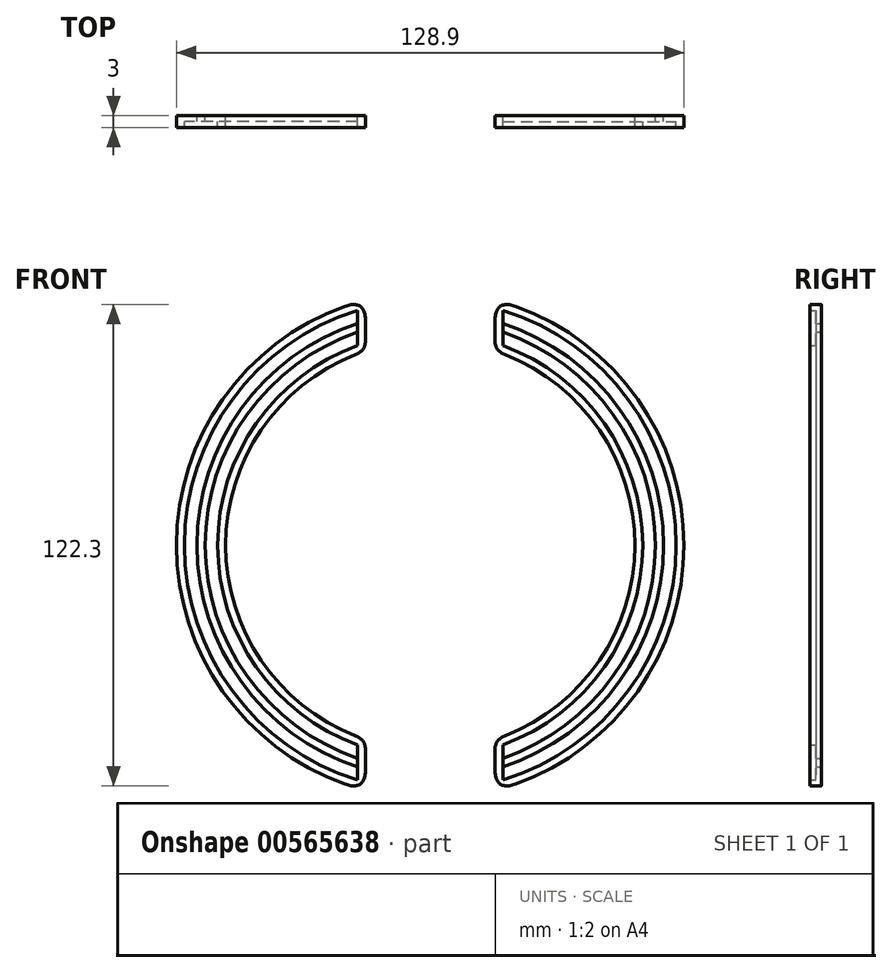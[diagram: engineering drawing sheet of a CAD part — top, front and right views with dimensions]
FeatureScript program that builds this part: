
annotation { "Feature Type Name" : "Feature", "Feature Type Description" : "" }
export const myFeature = defineFeature(function(context is Context, id is Id, definition is map)
    precondition{}
    {
        {
            var Q0;
            Q0=qCreatedBy(makeId("Front.planeOp"),FACE);
            var sketch = newSketch(context, id + "F0", { "sketchPlane" : qUnion([Q0])});
            skArc(sketch, "E0", {"start": v(-16.43, 51.43) * mm, "mid": v(-53.99, 0) * mm, "end": v(-16.43, -51.43) * mm, "construction": true});
            skLineSegment(sketch, "E1", {"start": v(53.99, 0) * mm, "end": v(-53.99, 0) * mm, "construction": true});
            skArc(sketch, "E2", {"start": v(-16.43, 51.43) * mm, "mid": v(-53.99, 0) * mm, "end": v(-16.43, -51.43) * mm});
            skArc(sketch, "E3.0", {"start": v(-16.43, 54.75) * mm, "mid": v(-57.16, 0) * mm, "end": v(-16.43, -54.75) * mm});
            skArc(sketch, "E4", {"start": v(16.43, -51.43) * mm, "mid": v(53.99, 0) * mm, "end": v(16.43, 51.43) * mm});
            skArc(sketch, "E5.0", {"start": v(16.43, -54.75) * mm, "mid": v(57.16, 0) * mm, "end": v(16.43, 54.75) * mm});
            skArc(sketch, "E6.0", {"start": v(-16.43, 56.96) * mm, "mid": v(-59.28, 0) * mm, "end": v(-16.43, -56.96) * mm});
            skArc(sketch, "E7.0", {"start": v(16.43, -56.96) * mm, "mid": v(59.28, 0) * mm, "end": v(16.43, 56.96) * mm});
            skArc(sketch, "E8.0", {"start": v(-16.43, 60.25) * mm, "mid": v(-62.45, 0) * mm, "end": v(-16.43, -60.25) * mm});
            skArc(sketch, "E8.1", {"start": v(16.43, -60.25) * mm, "mid": v(62.45, 0) * mm, "end": v(16.43, 60.25) * mm});
            skArc(sketch, "E9.0", {"start": v(-16.43, 49.32) * mm, "mid": v(-51.99, 0) * mm, "end": v(-16.43, -49.32) * mm});
            skArc(sketch, "E10.0", {"start": v(-16.43, 62.33) * mm, "mid": v(-64.45, 0) * mm, "end": v(-16.43, -62.33) * mm});
            skArc(sketch, "E11.MirrorCS", {"start": v(16.43, 51.43) * mm, "mid": v(53.99, 0) * mm, "end": v(16.43, -51.43) * mm});
            skArc(sketch, "E12.MirrorCS", {"start": v(16.43, 56.96) * mm, "mid": v(59.28, 0) * mm, "end": v(16.43, -56.96) * mm});
            skArc(sketch, "E13.MirrorCS", {"start": v(16.43, 62.33) * mm, "mid": v(64.45, 0) * mm, "end": v(16.43, -62.33) * mm});
            skArc(sketch, "E14.MirrorCS", {"start": v(16.43, 49.32) * mm, "mid": v(51.99, 0) * mm, "end": v(16.43, -49.32) * mm});
            skArc(sketch, "E15.MirrorCS", {"start": v(16.43, 60.25) * mm, "mid": v(62.45, 0) * mm, "end": v(16.43, -60.25) * mm});
            skArc(sketch, "E16.MirrorCS", {"start": v(16.43, 54.75) * mm, "mid": v(57.16, 0) * mm, "end": v(16.43, -54.75) * mm});
            skLineSegment(sketch, "E17.left", {"start": v(-16.43, 62.33) * mm, "end": v(-16.43, 49.32) * mm});
            skLineSegment(sketch, "E17.right", {"start": v(16.43, 62.33) * mm, "end": v(16.43, 49.32) * mm});
            skPoint(sketch, "E18.orphan", {"position": v(-16.43, 64.45) * mm});
            skLineSegment(sketch, "E19.trimOffspring", {"start": v(0, 0) * mm, "end": v(0, -53.99) * mm, "construction": true});
            skArc(sketch, "E20.trimOffspring", {"start": v(16.43, -51.43) * mm, "mid": v(53.99, 0) * mm, "end": v(16.43, 51.43) * mm, "construction": true});
            skLineSegment(sketch, "E21.trimOffspring", {"start": v(-16.43, -49.32) * mm, "end": v(-16.43, -62.33) * mm});
            skLineSegment(sketch, "E22.trimOffspring", {"start": v(16.43, -49.32) * mm, "end": v(16.43, -60.25) * mm});
            skLineSegment(sketch, "E23", {"start": v(16.43, -60.25) * mm, "end": v(16.43, -62.33) * mm});
            skLineSegment(sketch, "E24.right", {"start": v(-18.43, 61.76) * mm, "end": v(-18.43, 48.61) * mm});
            skLineSegment(sketch, "E25.MirrorCS", {"start": v(18.43, 61.76) * mm, "end": v(18.43, 48.61) * mm});
            skPoint(sketch, "E26.orphan", {"position": v(-18.43, -62.33) * mm});
            skPoint(sketch, "E27.orphan", {"position": v(18.43, -62.33) * mm});
            skPoint(sketch, "E28.orphan", {"position": v(-18.43, 62.33) * mm});
            skPoint(sketch, "E29.orphan", {"position": v(18.43, 62.33) * mm});
            skLineSegment(sketch, "E30.trimOffspring", {"start": v(-18.43, 0) * mm, "end": v(-18.43, -61.76) * mm});
            skLineSegment(sketch, "E31.trimOffspring", {"start": v(-16.43, 0) * mm, "end": v(-16.43, -62.33) * mm});
            skLineSegment(sketch, "E32.trimOffspring", {"start": v(16.43, 0) * mm, "end": v(16.43, -62.33) * mm});
            skLineSegment(sketch, "E33.trimOffspring", {"start": v(18.43, 0) * mm, "end": v(18.43, -61.76) * mm});
            skSolve(sketch);
        }
        {
            var Q0;
            {var subQ0=sQuery(id+"F0.wireOp",EDGE,"E6.0");Q0=makeQuery(id+"F0.imprint","IMPRINT",FACE,{"disambiguationData":[TD([[makeQuery(id+"F0.imprint","IMPRINT",EDGE,{"derivedFrom":subQ0}),-1.0]])]});}
            var Q1;
            {var subQ0=sQuery(id+"F0.wireOp",EDGE,"E2");Q1=makeQuery(id+"F0.imprint","IMPRINT",FACE,{"disambiguationData":[TD([[makeQuery(id+"F0.imprint","IMPRINT",EDGE,{"derivedFrom":subQ0}),-1.0]])]});}
            var Q2;
            {var subQ0=sQuery(id+"F0.wireOp",EDGE,"E7.0");Q2=makeQuery(id+"F0.imprint","IMPRINT",FACE,{"disambiguationData":[TD([[makeQuery(id+"F0.imprint","IMPRINT",EDGE,{"derivedFrom":subQ0}),-1.0]])]});}
            var Q3;
            {var subQ0=sQuery(id+"F0.wireOp",EDGE,"E4");Q3=makeQuery(id+"F0.imprint","IMPRINT",FACE,{"disambiguationData":[TD([[makeQuery(id+"F0.imprint","IMPRINT",EDGE,{"derivedFrom":subQ0}),-1.0]])]});}
            extrude(context, id + "F1", {"entities" : qUnion([Q0, Q1, Q2, Q3]), "depth" : 1.5 * mm, "offsetDistance" : 25 * mm});
        }
        {
            var Q0;
            {var subQ0=sQuery(id+"F0.wireOp",EDGE,"E8.0");Q0=makeQuery(id+"F0.imprint","IMPRINT",FACE,{"disambiguationData":[TD([[makeQuery(id+"F0.imprint","IMPRINT",EDGE,{"derivedFrom":subQ0}),-1.0]])]});}
            var Q1;
            {var subQ0=sQuery(id+"F0.wireOp",EDGE,"E2");Q1=makeQuery(id+"F0.imprint","IMPRINT",FACE,{"disambiguationData":[TD([[makeQuery(id+"F0.imprint","IMPRINT",EDGE,{"derivedFrom":subQ0}),1.0]])]});}
            var Q2;
            {var subQ0=sQuery(id+"F0.wireOp",EDGE,"E4");Q2=makeQuery(id+"F0.imprint","IMPRINT",FACE,{"disambiguationData":[TD([[makeQuery(id+"F0.imprint","IMPRINT",EDGE,{"derivedFrom":subQ0}),1.0]])]});}
            var Q3;
            {var subQ0=sQuery(id+"F0.wireOp",EDGE,"E8.1");Q3=makeQuery(id+"F0.imprint","IMPRINT",FACE,{"disambiguationData":[TD([[makeQuery(id+"F0.imprint","IMPRINT",EDGE,{"derivedFrom":subQ0}),-1.0]])]});}
            var Q4;
            {var subQ0=sQuery(id+"F0.wireOp",EDGE,"E17.left");var subQ1=sQuery(id+"F0.wireOp",EDGE,"E3.0");var subQ2=makeQuery(id+"F0.imprint","INTERSECT",VERTEX,{"derivedFrom":[subQ1,subQ0]});Q4=makeQuery(id+"F0.imprint","IMPRINT",FACE,{"disambiguationData":[TD([[makeQuery(id+"F0.imprint","IMPRINT",EDGE,{"disambiguationData":[TD([[subQ2,-1.0]])],"derivedFrom":subQ1}),-1.0]])]});}
            var Q5;
            {var subQ0=sQuery(id+"F0.wireOp",EDGE,"E17.right");var subQ1=sQuery(id+"F0.wireOp",EDGE,"E5.0");var subQ2=makeQuery(id+"F0.imprint","INTERSECT",VERTEX,{"derivedFrom":[subQ1,subQ0]});Q5=makeQuery(id+"F0.imprint","IMPRINT",FACE,{"disambiguationData":[TD([[makeQuery(id+"F0.imprint","IMPRINT",EDGE,{"disambiguationData":[TD([[subQ2,1.0]])],"derivedFrom":subQ1}),-1.0]])]});}
            var Q6;
            {var subQ0=sQuery(id+"F0.wireOp",EDGE,"E17.left");var subQ1=sQuery(id+"F0.wireOp",EDGE,"E2");var subQ2=makeQuery(id+"F0.imprint","INTERSECT",VERTEX,{"derivedFrom":[subQ1,subQ0]});Q6=makeQuery(id+"F0.imprint","IMPRINT",FACE,{"disambiguationData":[TD([[makeQuery(id+"F0.imprint","IMPRINT",EDGE,{"disambiguationData":[TD([[subQ2,-1.0]])],"derivedFrom":subQ1}),-1.0]])]});}
            var Q7;
            {var subQ0=sQuery(id+"F0.wireOp",EDGE,"E17.left");var subQ1=sQuery(id+"F0.wireOp",EDGE,"E6.0");var subQ2=makeQuery(id+"F0.imprint","INTERSECT",VERTEX,{"derivedFrom":[subQ1,subQ0]});Q7=makeQuery(id+"F0.imprint","IMPRINT",FACE,{"disambiguationData":[TD([[makeQuery(id+"F0.imprint","IMPRINT",EDGE,{"disambiguationData":[TD([[subQ2,-1.0]])],"derivedFrom":subQ1}),-1.0]])]});}
            var Q8;
            {var subQ0=sQuery(id+"F0.wireOp",EDGE,"E17.right");var subQ1=sQuery(id+"F0.wireOp",EDGE,"E7.0");var subQ2=makeQuery(id+"F0.imprint","INTERSECT",VERTEX,{"derivedFrom":[subQ1,subQ0]});Q8=makeQuery(id+"F0.imprint","IMPRINT",FACE,{"disambiguationData":[TD([[makeQuery(id+"F0.imprint","IMPRINT",EDGE,{"disambiguationData":[TD([[subQ2,1.0]])],"derivedFrom":subQ1}),-1.0]])]});}
            var Q9;
            {var subQ0=sQuery(id+"F0.wireOp",EDGE,"E17.right");var subQ1=sQuery(id+"F0.wireOp",EDGE,"E4");var subQ2=makeQuery(id+"F0.imprint","INTERSECT",VERTEX,{"derivedFrom":[subQ1,subQ0]});Q9=makeQuery(id+"F0.imprint","IMPRINT",FACE,{"disambiguationData":[TD([[makeQuery(id+"F0.imprint","IMPRINT",EDGE,{"disambiguationData":[TD([[subQ2,1.0]])],"derivedFrom":subQ1}),-1.0]])]});}
            var Q10;
            {var subQ0=sQuery(id+"F0.wireOp",EDGE,"E21.trimOffspring");var subQ1=sQuery(id+"F0.wireOp",EDGE,"E2");var subQ2=makeQuery(id+"F0.imprint","INTERSECT",VERTEX,{"derivedFrom":[subQ1,subQ0]});Q10=makeQuery(id+"F0.imprint","IMPRINT",FACE,{"disambiguationData":[TD([[makeQuery(id+"F0.imprint","IMPRINT",EDGE,{"disambiguationData":[TD([[subQ2,1.0]])],"derivedFrom":subQ1}),-1.0]])]});}
            var Q11;
            {var subQ0=sQuery(id+"F0.wireOp",EDGE,"E21.trimOffspring");var subQ1=sQuery(id+"F0.wireOp",EDGE,"E3.0");var subQ2=makeQuery(id+"F0.imprint","INTERSECT",VERTEX,{"derivedFrom":[subQ1,subQ0]});Q11=makeQuery(id+"F0.imprint","IMPRINT",FACE,{"disambiguationData":[TD([[makeQuery(id+"F0.imprint","IMPRINT",EDGE,{"disambiguationData":[TD([[subQ2,1.0]])],"derivedFrom":subQ1}),-1.0]])]});}
            var Q12;
            {var subQ0=sQuery(id+"F0.wireOp",EDGE,"E21.trimOffspring");var subQ1=sQuery(id+"F0.wireOp",EDGE,"E6.0");var subQ2=makeQuery(id+"F0.imprint","INTERSECT",VERTEX,{"derivedFrom":[subQ1,subQ0]});Q12=makeQuery(id+"F0.imprint","IMPRINT",FACE,{"disambiguationData":[TD([[makeQuery(id+"F0.imprint","IMPRINT",EDGE,{"disambiguationData":[TD([[subQ2,1.0]])],"derivedFrom":subQ1}),-1.0]])]});}
            var Q13;
            {var subQ0=sQuery(id+"F0.wireOp",EDGE,"E22.trimOffspring");var subQ1=sQuery(id+"F0.wireOp",EDGE,"E5.0");var subQ2=makeQuery(id+"F0.imprint","INTERSECT",VERTEX,{"derivedFrom":[subQ1,subQ0]});Q13=makeQuery(id+"F0.imprint","IMPRINT",FACE,{"disambiguationData":[TD([[makeQuery(id+"F0.imprint","IMPRINT",EDGE,{"disambiguationData":[TD([[subQ2,-1.0]])],"derivedFrom":subQ1}),-1.0]])]});}
            var Q14;
            {var subQ0=sQuery(id+"F0.wireOp",EDGE,"E22.trimOffspring");var subQ1=sQuery(id+"F0.wireOp",EDGE,"E4");var subQ2=makeQuery(id+"F0.imprint","INTERSECT",VERTEX,{"derivedFrom":[subQ1,subQ0]});Q14=makeQuery(id+"F0.imprint","IMPRINT",FACE,{"disambiguationData":[TD([[makeQuery(id+"F0.imprint","IMPRINT",EDGE,{"disambiguationData":[TD([[subQ2,-1.0]])],"derivedFrom":subQ1}),-1.0]])]});}
            var Q15;
            {var subQ0=sQuery(id+"F0.wireOp",EDGE,"E22.trimOffspring");var subQ1=sQuery(id+"F0.wireOp",EDGE,"E7.0");var subQ2=makeQuery(id+"F0.imprint","INTERSECT",VERTEX,{"derivedFrom":[subQ1,subQ0]});Q15=makeQuery(id+"F0.imprint","IMPRINT",FACE,{"disambiguationData":[TD([[makeQuery(id+"F0.imprint","IMPRINT",EDGE,{"disambiguationData":[TD([[subQ2,-1.0]])],"derivedFrom":subQ1}),-1.0]])]});}
            extrude(context, id + "F2", {"entities" : qUnion([Q0, Q1, Q2, Q3, Q4, Q5, Q6, Q7, Q8, Q9, Q10, Q11, Q12, Q13, Q14, Q15]), "operationType" : NewBodyOperationType.ADD, "depth" : 3 * mm, "offsetDistance" : 25 * mm});
        }
        {
            var Q0;
            Q0=makeQuery(id+"F2.opExtrude","SWEPT_EDGE",EDGE,{"disambiguationData":[OSD([sQuery(id+"F0.wireOp",EDGE,"E13.MirrorCS"),sQuery(id+"F0.wireOp",EDGE,"E17.right")])]});
            var Q1;
            Q1=makeQuery(id+"F2.opExtrude","SWEPT_EDGE",EDGE,{"disambiguationData":[OSD([sQuery(id+"F0.wireOp",EDGE,"E10.0"),sQuery(id+"F0.wireOp",EDGE,"E21.trimOffspring")])]});
            var Q2;
            Q2=makeQuery(id+"F2.opExtrude","SWEPT_EDGE",EDGE,{"disambiguationData":[OSD([sQuery(id+"F0.wireOp",EDGE,"E9.0"),sQuery(id+"F0.wireOp",EDGE,"E21.trimOffspring")])]});
            var Q3;
            Q3=makeQuery(id+"F2.opExtrude","SWEPT_EDGE",EDGE,{"disambiguationData":[OSD([sQuery(id+"F0.wireOp",EDGE,"E14.MirrorCS"),sQuery(id+"F0.wireOp",EDGE,"E22.trimOffspring")])]});
            var Q4;
            Q4=makeQuery(id+"F2.opExtrude","SWEPT_EDGE",EDGE,{"disambiguationData":[OSD([sQuery(id+"F0.wireOp",EDGE,"E13.MirrorCS"),sQuery(id+"F0.wireOp",EDGE,"E23")])]});
            var Q5;
            Q5=makeQuery(id+"F2.opExtrude","SWEPT_EDGE",EDGE,{"disambiguationData":[OSD([sQuery(id+"F0.wireOp",EDGE,"E14.MirrorCS"),sQuery(id+"F0.wireOp",EDGE,"E17.right")])]});
            var Q6;
            Q6=makeQuery(id+"F2.opExtrude","SWEPT_EDGE",EDGE,{"disambiguationData":[OSD([sQuery(id+"F0.wireOp",EDGE,"E10.0"),sQuery(id+"F0.wireOp",EDGE,"E17.left")])]});
            var Q7;
            Q7=makeQuery(id+"F2.opExtrude","SWEPT_EDGE",EDGE,{"disambiguationData":[OSD([sQuery(id+"F0.wireOp",EDGE,"E9.0"),sQuery(id+"F0.wireOp",EDGE,"E17.left")])]});
            fillet(context, id + "F3", {"entities" : qUnion([Q0, Q1, Q2, Q3, Q4, Q5, Q6, Q7]), "tangentPropagation" : true, "crossSection" : FilletCrossSection.CONIC, "radius" : 4 * mm, "rho" : 0.5, "defaultsChanged" : false, "vertexSettings" : [], "allowEdgeOverflow" : false});
        }
    });
